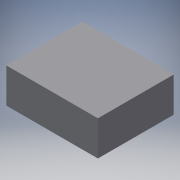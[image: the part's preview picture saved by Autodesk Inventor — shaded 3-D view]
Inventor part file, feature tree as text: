
AUTODESK INVENTOR PART (.ipt)
format: ipt  version: 2018 (Build 220112000, 112)  size: 84,480 bytes
history: native  units: mm
features: extrude x1, sketch x1
ambient origin geometry x8: Origin, YZ Plane, XZ Plane, XY Plane, X Axis, Y Axis, Z Axis, Center Point
bodies: Solid1 (feature_tree)
feature tree (2):
  extrude  "Extrusion1"  Depth=48.0mm
  sketch  "Sketch1"  dims[d0=58.0mm d1=48.0mm d2=22.0mm d3=0.0mm]
